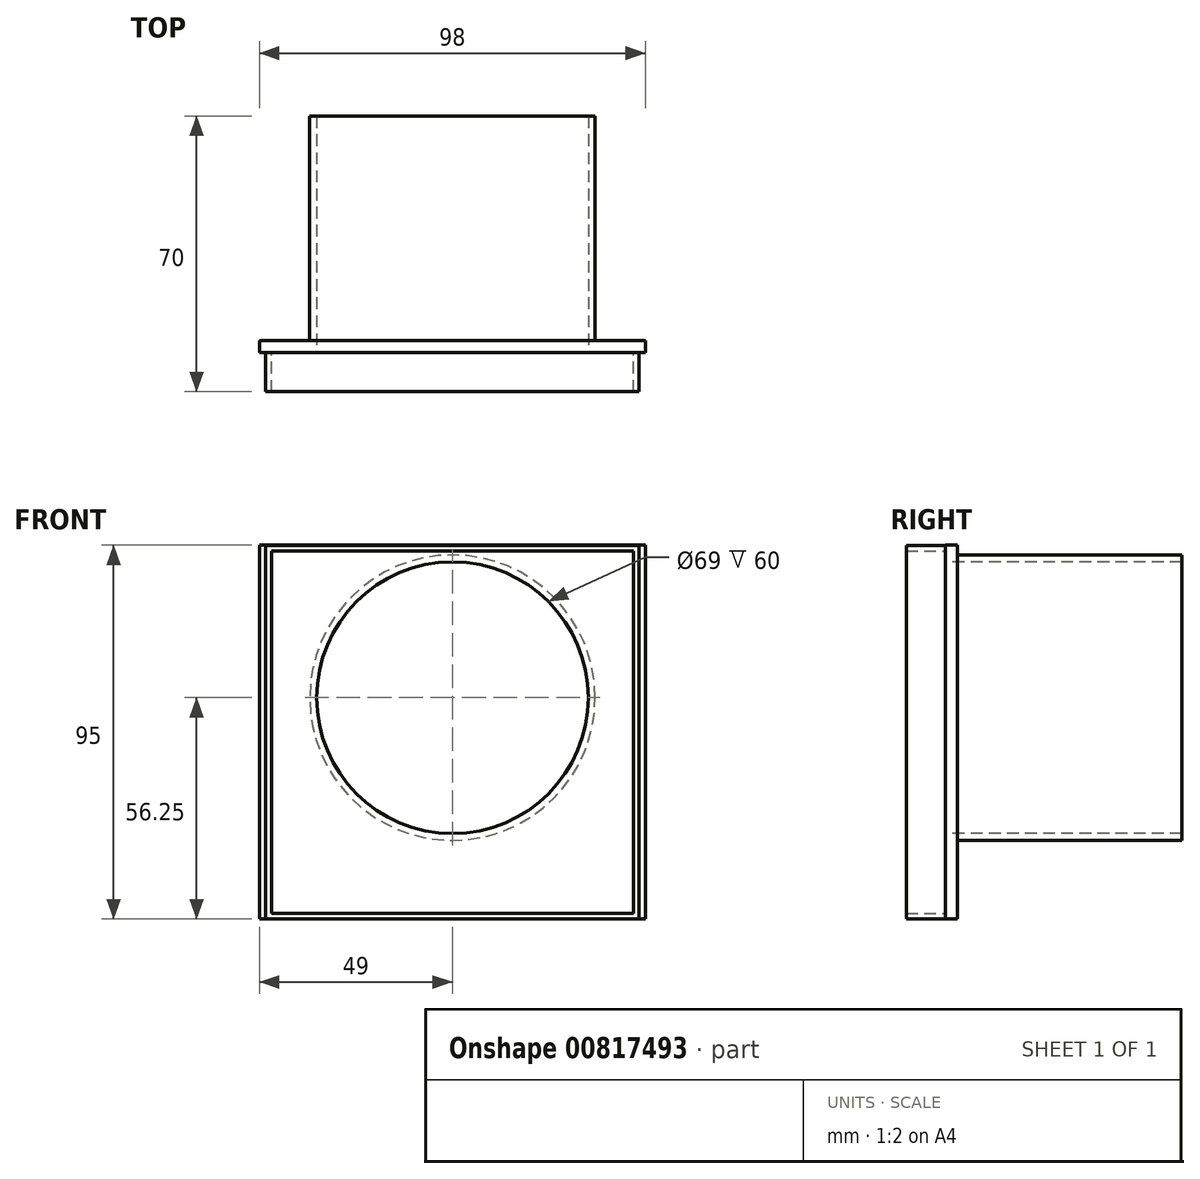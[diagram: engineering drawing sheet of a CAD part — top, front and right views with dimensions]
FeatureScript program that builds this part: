
annotation { "Feature Type Name" : "Feature", "Feature Type Description" : "" }
export const myFeature = defineFeature(function(context is Context, id is Id, definition is map)
    precondition{}
    {
        {
            var Q0;
            Q0=qCreatedBy(makeId("Front.planeOp"),FACE);
            var sketch = newSketch(context, id + "F0", { "sketchPlane" : qUnion([Q0])});
            skLineSegment(sketch, "E0.bottom", {"start": v(49, -47.5) * mm, "end": v(-49, -47.5) * mm});
            skLineSegment(sketch, "E0.top", {"start": v(49, 47.5) * mm, "end": v(-49, 47.5) * mm});
            skLineSegment(sketch, "E0.left", {"start": v(49, -47.5) * mm, "end": v(49, 47.5) * mm});
            skLineSegment(sketch, "E0.right", {"start": v(-49, -47.5) * mm, "end": v(-49, 47.5) * mm});
            skPoint(sketch, "E0.middle", {"position": v(0, 0) * mm});
            skSolve(sketch);
        }
        {
            var Q0;
            Q0=makeQuery(id+"F0.imprint","IMPRINT",FACE,{"disambiguationData":[TD([[makeQuery(id+"F0.imprint","IMPRINT",EDGE,{"derivedFrom":sQuery(id+"F0.wireOp",EDGE,"E0.bottom")}),-1.0]])]});
            extrude(context, id + "F1", {"entities" : qUnion([Q0]), "oppositeDirection" : true, "depth" : 3 * mm, "offsetDistance" : 25 * mm});
        }
        {
            var Q0;
            Q0=qCreatedBy(makeId("Front.planeOp"),FACE);
            var sketch = newSketch(context, id + "F2", { "sketchPlane" : qUnion([Q0])});
            skCircle(sketch, "E1", {"center": v(0, 8.75) * mm, "radius": 33.25 * mm});
            skCircle(sketch, "E2.0", {"center": v(0, 8.75) * mm, "radius": 36.25 * mm});
            skSolve(sketch);
        }
        {
            var Q0;
            Q0=makeQuery(id+"F2.imprint","IMPRINT",FACE,{"disambiguationData":[TD([[makeQuery(id+"F2.imprint","IMPRINT",EDGE,{"derivedFrom":sQuery(id+"F2.wireOp",EDGE,"E1")}),1.0]])]});
            var Q1;
            Q1=makeQuery(id+"F2.imprint","IMPRINT",FACE,{"disambiguationData":[TD([[makeQuery(id+"F2.imprint","IMPRINT",EDGE,{"derivedFrom":sQuery(id+"F2.wireOp",EDGE,"E1")}),-1.0]])]});
            extrude(context, id + "F3", {"entities" : qUnion([Q0, Q1]), "operationType" : NewBodyOperationType.REMOVE, "oppositeDirection" : true, "depth" : 4 * mm, "offsetDistance" : 25 * mm});
        }
        {
            var Q0;
            Q0=makeQuery(id+"F1.opExtrude","CAP_FACE",FACE,{"disambiguationData":[OSD([sQuery(id+"F0.wireOp",EDGE,"E0.bottom"),sQuery(id+"F0.wireOp",EDGE,"E0.top"),sQuery(id+"F0.wireOp",EDGE,"E0.left"),sQuery(id+"F0.wireOp",EDGE,"E0.right")])],"isStart":true});
            var sketch = newSketch(context, id + "F4", { "sketchPlane" : qUnion([Q0])});
            skCircle(sketch, "E3", {"center": v(0, 8.75) * mm, "radius": 34.5 * mm});
            skSolve(sketch);
        }
        {
            var Q0;
            Q0=makeQuery(id+"F4.imprint","IMPRINT",FACE,{"disambiguationData":[TD([[makeQuery(id+"F4.imprint","IMPRINT",EDGE,{"derivedFrom":sQuery(id+"F4.wireOp",EDGE,"E3")}),-1.0]])]});
            extrude(context, id + "F5", {"entities" : qUnion([Q0]), "operationType" : NewBodyOperationType.ADD, "oppositeDirection" : true, "depth" : 60 * mm, "offsetDistance" : 25 * mm});
        }
        {
            var Q0;
            Q0=qCreatedBy(makeId("Front.planeOp"),FACE);
            var sketch = newSketch(context, id + "F6", { "sketchPlane" : qUnion([Q0])});
            skLineSegment(sketch, "E4.bottom", {"start": v(47.44, -47.44) * mm, "end": v(-47.44, -47.44) * mm});
            skLineSegment(sketch, "E4.top", {"start": v(47.44, 47.44) * mm, "end": v(-47.44, 47.44) * mm});
            skLineSegment(sketch, "E4.left", {"start": v(47.44, -47.44) * mm, "end": v(47.44, 47.44) * mm});
            skLineSegment(sketch, "E4.right", {"start": v(-47.44, -47.44) * mm, "end": v(-47.44, 47.44) * mm});
            skPoint(sketch, "E4.middle", {"position": v(0, 0) * mm});
            skLineSegment(sketch, "E5.bottom", {"start": v(46, -46) * mm, "end": v(-46, -46) * mm});
            skLineSegment(sketch, "E5.top", {"start": v(46, 46) * mm, "end": v(-46, 46) * mm});
            skLineSegment(sketch, "E5.left", {"start": v(46, -46) * mm, "end": v(46, 46) * mm});
            skLineSegment(sketch, "E5.right", {"start": v(-46, -46) * mm, "end": v(-46, 46) * mm});
            skSolve(sketch);
        }
        {
            var Q0;
            Q0=makeQuery(id+"F6.imprint","IMPRINT",FACE,{"disambiguationData":[TD([[makeQuery(id+"F6.imprint","IMPRINT",EDGE,{"derivedFrom":sQuery(id+"F6.wireOp",EDGE,"E4.bottom")}),-1.0]])]});
            extrude(context, id + "F7", {"entities" : qUnion([Q0]), "operationType" : NewBodyOperationType.ADD, "depth" : 10 * mm, "offsetDistance" : 25 * mm});
        }
    });
